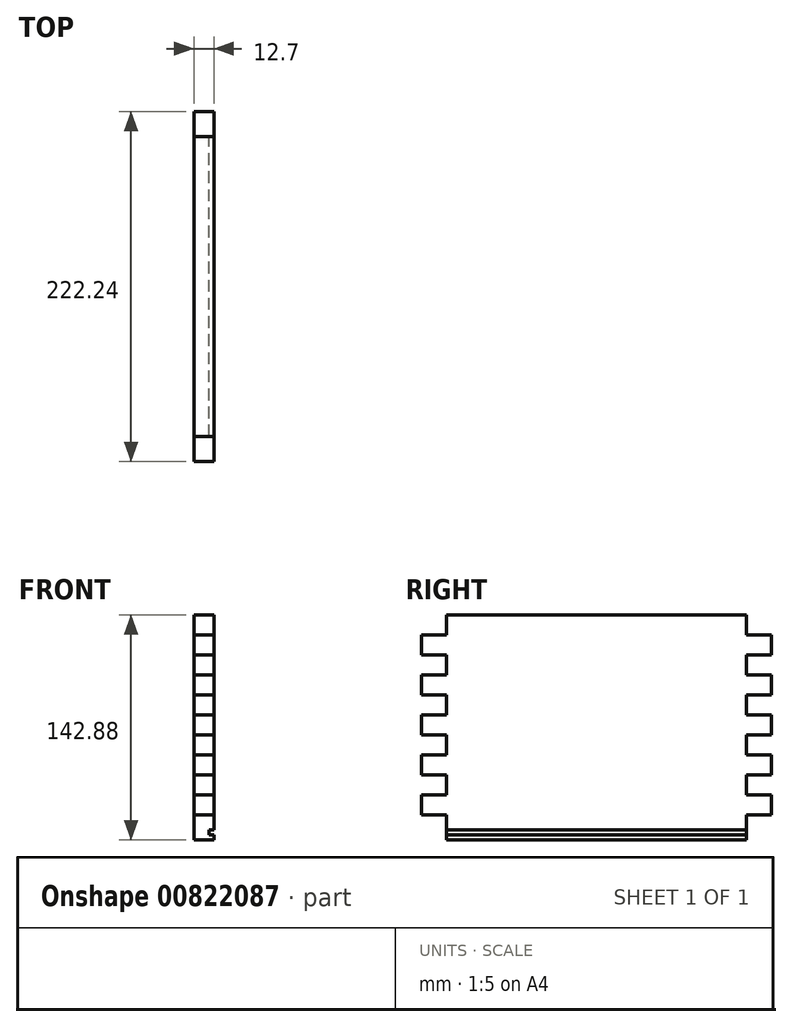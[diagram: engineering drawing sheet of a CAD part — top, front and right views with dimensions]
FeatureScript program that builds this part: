
annotation { "Feature Type Name" : "Feature", "Feature Type Description" : "" }
export const myFeature = defineFeature(function(context is Context, id is Id, definition is map)
    precondition{}
    {
        {
            var Q0;
            Q0=qCreatedBy(makeId("Right.planeOp"),FACE);
            var sketch = newSketch(context, id + "F0", { "sketchPlane" : qUnion([Q0])});
            skLineSegment(sketch, "E0.bottom", {"start": v(-95.25, -73.03) * mm, "end": v(95.25, -73.03) * mm});
            skLineSegment(sketch, "E0.top", {"start": v(-95.25, 69.85) * mm, "end": v(95.25, 69.85) * mm});
            skLineSegment(sketch, "E0.left", {"start": v(-111.13, -57.15) * mm, "end": v(-111.13, -44.45) * mm});
            skLineSegment(sketch, "E0.right", {"start": v(111.13, -57.15) * mm, "end": v(111.13, -44.45) * mm});
            skPoint(sketch, "E0.middle", {"position": v(0, 0) * mm});
            skLineSegment(sketch, "E1.top", {"start": v(-111.13, -57.15) * mm, "end": v(-95.25, -57.15) * mm});
            skLineSegment(sketch, "E1.right", {"start": v(-95.25, -73.03) * mm, "end": v(-95.25, -57.15) * mm});
            skLineSegment(sketch, "E2.0.1.0", {"start": v(-111.13, -31.75) * mm, "end": v(-95.25, -31.75) * mm});
            skLineSegment(sketch, "E2.0.1.1", {"start": v(-111.13, -44.45) * mm, "end": v(-95.25, -44.45) * mm});
            skLineSegment(sketch, "E2.0.1.3", {"start": v(-95.25, -44.45) * mm, "end": v(-95.25, -31.75) * mm});
            skLineSegment(sketch, "E2.0.2.0", {"start": v(-111.13, -6.35) * mm, "end": v(-95.25, -6.35) * mm});
            skLineSegment(sketch, "E2.0.2.1", {"start": v(-111.13, -19.05) * mm, "end": v(-95.25, -19.05) * mm});
            skLineSegment(sketch, "E2.0.2.3", {"start": v(-95.25, -19.05) * mm, "end": v(-95.25, -6.35) * mm});
            skLineSegment(sketch, "E2.0.3.0", {"start": v(-111.13, 19.05) * mm, "end": v(-95.25, 19.05) * mm});
            skLineSegment(sketch, "E2.0.3.1", {"start": v(-111.13, 6.35) * mm, "end": v(-95.25, 6.35) * mm});
            skLineSegment(sketch, "E2.0.3.3", {"start": v(-95.25, 6.35) * mm, "end": v(-95.25, 19.05) * mm});
            skLineSegment(sketch, "E2.0.4.0", {"start": v(-111.13, 44.45) * mm, "end": v(-95.25, 44.45) * mm});
            skLineSegment(sketch, "E2.0.4.1", {"start": v(-111.13, 31.75) * mm, "end": v(-95.25, 31.75) * mm});
            skLineSegment(sketch, "E2.0.4.3", {"start": v(-95.25, 31.75) * mm, "end": v(-95.25, 44.45) * mm});
            skLineSegment(sketch, "E2.0.5.1", {"start": v(-111.13, 57.15) * mm, "end": v(-95.25, 57.15) * mm});
            skLineSegment(sketch, "E2.0.5.3", {"start": v(-95.25, 57.15) * mm, "end": v(-95.25, 69.85) * mm});
            skLineSegment(sketch, "E2.direction2", {"start": v(-111.13, -57.15) * mm, "end": v(-111.13, -44.45) * mm, "construction": true});
            skLineSegment(sketch, "E3.MirrorCS", {"start": v(111.13, 19.05) * mm, "end": v(95.25, 19.05) * mm});
            skLineSegment(sketch, "E4.MirrorCS", {"start": v(111.13, 44.45) * mm, "end": v(95.25, 44.45) * mm});
            skLineSegment(sketch, "E5.MirrorCS", {"start": v(95.25, 31.75) * mm, "end": v(95.25, 44.45) * mm});
            skLineSegment(sketch, "E6.MirrorCS", {"start": v(111.13, 57.15) * mm, "end": v(95.25, 57.15) * mm});
            skLineSegment(sketch, "E7.MirrorCS", {"start": v(95.25, 57.15) * mm, "end": v(95.25, 69.85) * mm});
            skLineSegment(sketch, "E8.MirrorCS", {"start": v(111.13, -6.35) * mm, "end": v(95.25, -6.35) * mm});
            skLineSegment(sketch, "E9.MirrorCS", {"start": v(95.25, -44.45) * mm, "end": v(95.25, -31.75) * mm});
            skLineSegment(sketch, "E10.MirrorCS", {"start": v(111.13, -44.45) * mm, "end": v(95.25, -44.45) * mm});
            skLineSegment(sketch, "E11.MirrorCS", {"start": v(111.13, -31.75) * mm, "end": v(95.25, -31.75) * mm});
            skLineSegment(sketch, "E12.MirrorCS", {"start": v(95.25, -73.03) * mm, "end": v(95.25, -57.15) * mm});
            skLineSegment(sketch, "E13.MirrorCS", {"start": v(111.13, -57.15) * mm, "end": v(95.25, -57.15) * mm});
            skLineSegment(sketch, "E14.MirrorCS", {"start": v(95.25, -19.05) * mm, "end": v(95.25, -6.35) * mm});
            skLineSegment(sketch, "E15.MirrorCS", {"start": v(111.13, 6.35) * mm, "end": v(95.25, 6.35) * mm});
            skLineSegment(sketch, "E16.MirrorCS", {"start": v(111.13, -19.05) * mm, "end": v(95.25, -19.05) * mm});
            skLineSegment(sketch, "E17.MirrorCS", {"start": v(95.25, 6.35) * mm, "end": v(95.25, 19.05) * mm});
            skLineSegment(sketch, "E18.MirrorCS", {"start": v(111.13, 31.75) * mm, "end": v(95.25, 31.75) * mm});
            skLineSegment(sketch, "E19.trimOffspring", {"start": v(-111.13, -31.75) * mm, "end": v(-111.13, -19.05) * mm});
            skLineSegment(sketch, "E20.trimOffspring", {"start": v(-111.13, -6.35) * mm, "end": v(-111.13, 6.35) * mm});
            skLineSegment(sketch, "E21.trimOffspring", {"start": v(-111.13, 19.05) * mm, "end": v(-111.13, 31.75) * mm});
            skLineSegment(sketch, "E22.trimOffspring", {"start": v(-111.13, 44.45) * mm, "end": v(-111.13, 57.15) * mm});
            skLineSegment(sketch, "E23.trimOffspring", {"start": v(111.13, 44.45) * mm, "end": v(111.13, 57.15) * mm});
            skLineSegment(sketch, "E24.trimOffspring", {"start": v(111.13, 19.05) * mm, "end": v(111.13, 31.75) * mm});
            skLineSegment(sketch, "E25.trimOffspring", {"start": v(111.13, -6.35) * mm, "end": v(111.13, 6.35) * mm});
            skLineSegment(sketch, "E26.trimOffspring", {"start": v(111.13, -31.75) * mm, "end": v(111.13, -19.05) * mm});
            skLineSegment(sketch, "E27.bottom", {"start": v(-95.25, -69.85) * mm, "end": v(95.25, -69.85) * mm});
            skLineSegment(sketch, "E27.top", {"start": v(-95.25, -66.68) * mm, "end": v(95.25, -66.68) * mm});
            skLineSegment(sketch, "E27.left", {"start": v(-95.25, -69.85) * mm, "end": v(-95.25, -66.68) * mm});
            skLineSegment(sketch, "E27.right", {"start": v(95.25, -69.85) * mm, "end": v(95.25, -66.68) * mm});
            skSolve(sketch);
        }
        {
            var Q0;
            Q0=makeQuery(id+"F0.imprint","IMPRINT",FACE,{"disambiguationData":[TD([[makeQuery(id+"F0.imprint","IMPRINT",EDGE,{"derivedFrom":sQuery(id+"F0.wireOp",EDGE,"E27.bottom")}),1.0]])]});
            extrude(context, id + "F1", {"entities" : qUnion([Q0]), "depth" : 9.52 * mm, "offsetDistance" : 25.4 * mm});
        }
        {
            var Q0;
            Q0=makeQuery(id+"F0.imprint","IMPRINT",FACE,{"disambiguationData":[TD([[makeQuery(id+"F0.imprint","IMPRINT",EDGE,{"derivedFrom":sQuery(id+"F0.wireOp",EDGE,"E0.top")}),-1.0]])]});
            var Q1;
            {var subQ0=sQuery(id+"F0.wireOp",EDGE,"E0.bottom");Q1=makeQuery(id+"F0.imprint","IMPRINT",FACE,{"disambiguationData":[TD([[makeQuery(id+"F0.imprint","IMPRINT",EDGE,{"derivedFrom":subQ0}),1.0]])]});}
            extrude(context, id + "F2", {"entities" : qUnion([Q0, Q1]), "operationType" : NewBodyOperationType.ADD, "depth" : 12.7 * mm, "offsetDistance" : 25.4 * mm});
        }
    });
